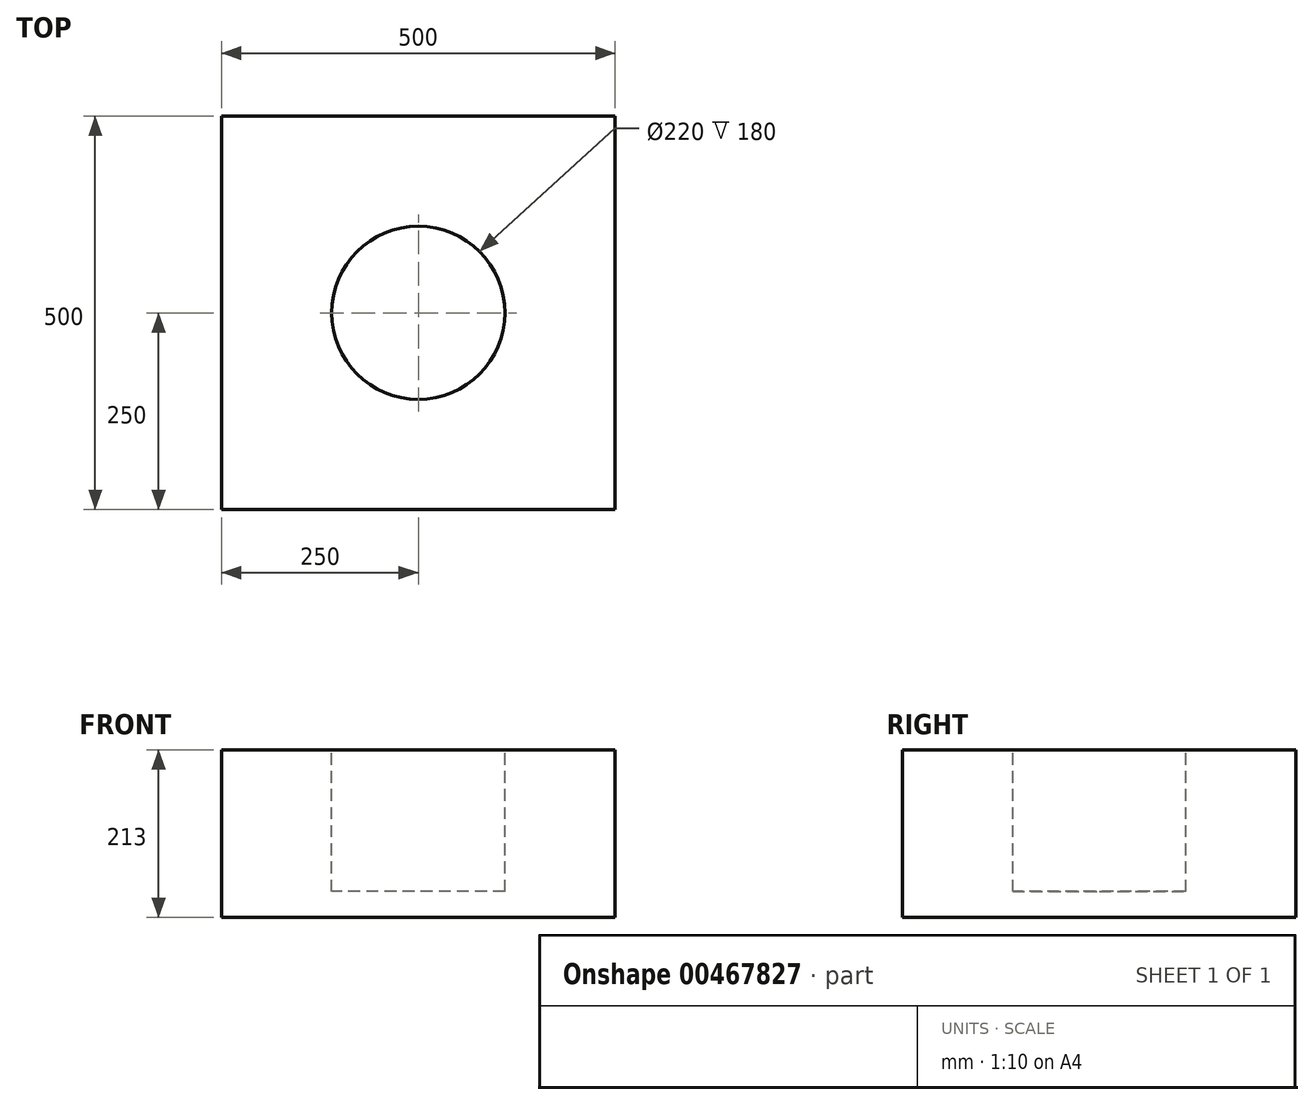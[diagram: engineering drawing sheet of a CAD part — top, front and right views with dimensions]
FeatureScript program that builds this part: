
annotation { "Feature Type Name" : "Feature", "Feature Type Description" : "" }
export const myFeature = defineFeature(function(context is Context, id is Id, definition is map)
    precondition{}
    {
        {
            var Q0;
            Q0=qCreatedBy(makeId("Top.planeOp"),FACE);
            var sketch = newSketch(context, id + "F0", { "sketchPlane" : qUnion([Q0])});
            skLineSegment(sketch, "E0.bottom", {"start": v(-250, -250) * mm, "end": v(250, -250) * mm});
            skLineSegment(sketch, "E0.top", {"start": v(-250, 250) * mm, "end": v(250, 250) * mm});
            skLineSegment(sketch, "E0.left", {"start": v(-250, -250) * mm, "end": v(-250, 250) * mm});
            skLineSegment(sketch, "E0.right", {"start": v(250, -250) * mm, "end": v(250, 250) * mm});
            skPoint(sketch, "E0.middle", {"position": v(0, 0) * mm});
            skSolve(sketch);
        }
        {
            var Q0;
            Q0=makeQuery(id+"F0.imprint","IMPRINT",FACE,{"disambiguationData":[TD([[makeQuery(id+"F0.imprint","IMPRINT",EDGE,{"derivedFrom":sQuery(id+"F0.wireOp",EDGE,"E0.bottom")}),1.0]])]});
            extrude(context, id + "F1", {"entities" : qUnion([Q0]), "depth" : 213 * mm, "offsetDistance" : 25 * mm});
        }
        {
            var Q0;
            Q0=makeQuery(id+"F1.opExtrude","CAP_FACE",FACE,{"disambiguationData":[OSD([sQuery(id+"F0.wireOp",EDGE,"E0.bottom"),sQuery(id+"F0.wireOp",EDGE,"E0.top"),sQuery(id+"F0.wireOp",EDGE,"E0.left"),sQuery(id+"F0.wireOp",EDGE,"E0.right")])],"isStart":false});
            var sketch = newSketch(context, id + "F2", { "sketchPlane" : qUnion([Q0])});
            skCircle(sketch, "E1", {"center": v(0, 0) * mm, "radius": 110 * mm});
            skSolve(sketch);
        }
        {
            var Q0;
            Q0=makeQuery(id+"F2.imprint","IMPRINT",FACE,{"disambiguationData":[TD([[makeQuery(id+"F2.imprint","IMPRINT",EDGE,{"derivedFrom":sQuery(id+"F2.wireOp",EDGE,"E1")}),1.0]])]});
            extrude(context, id + "F3", {"entities" : qUnion([Q0]), "operationType" : NewBodyOperationType.REMOVE, "oppositeDirection" : true, "depth" : 180 * mm});
        }
    });
